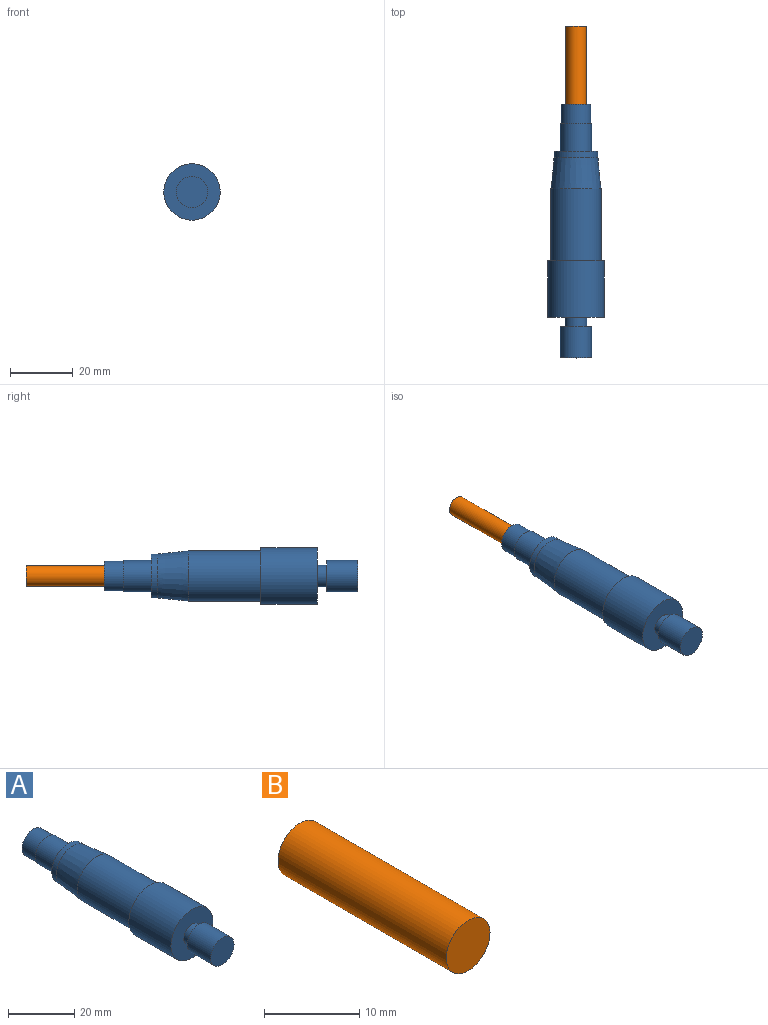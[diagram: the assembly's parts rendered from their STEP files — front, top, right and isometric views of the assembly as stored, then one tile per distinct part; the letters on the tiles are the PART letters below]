
ASSEMBLY  parts=2 mates=1
PART A: 15 faces, bbox 18x81x18 mm
  f0: plane 10x10mm, normal (0,-1,0), area 78.5mm2, adj f1
  f1: cylinder r=5mm len=10mm, axis (0,-1,0), area 314.2mm2, adj f0,f2
  f2: plane 10x10mm, normal (0,1,0), area 40.1mm2, adj f1,f3
  f3: cylinder r=3.5mm len=7mm, axis (0,-1,0), area 66mm2, adj f2,f4
  f4: plane 18x18mm, normal (0,-1,0), area 216mm2, adj f3,f5
  f5: cylinder r=9mm len=18mm, axis (0,-1,0), area 1017.9mm2, adj f4,f6
  f6: plane 18x18mm, normal (0,1,0), area 53.4mm2, adj f5,f7
  f7: cylinder r=8mm len=23mm, axis (0,-1,0), area 1156.1mm2, adj f6,f8
  f8: cone r=7mm half-angle=5.7deg, axis (0,-1,0), area 473.6mm2, adj f7,f9
  f9: cylinder r=7mm len=14mm, axis (0,-1,0), area 88mm2, adj f8,f10
  f10: plane 14x14mm, normal (0,1,0), area 75.4mm2, adj f9,f11
  f11: cylinder r=5mm len=10mm, axis (0,-1,0), area 282.7mm2, adj f10,f12
  f12: plane 10x10mm, normal (0,1,0), area 7.7mm2, adj f11,f13
  f13: cylinder r=4.75mm len=9.5mm, axis (0,-1,0), area 179.1mm2, adj f12,f14
  f14: plane 9.5x9.5mm, normal (0,1,0), area 70.9mm2, adj f13
PART B: 3 faces, bbox 6.5x25x6.5 mm
  f0: cylinder r=3.25mm len=25mm, axis (0,-1,0), area 510.5mm2, adj f1,f2
  f1: plane 6.5x6.5mm, normal (0,1,0), area 33.2mm2, adj f0
  f2: plane 6.5x6.5mm, normal (0,-1,0), area 33.2mm2, adj f0
PLACE A at identity fixed
PLACE B at identity
MATE slider B.f0 <-> A.f1  axis (0,-1,0) through (0,0,0)mm
